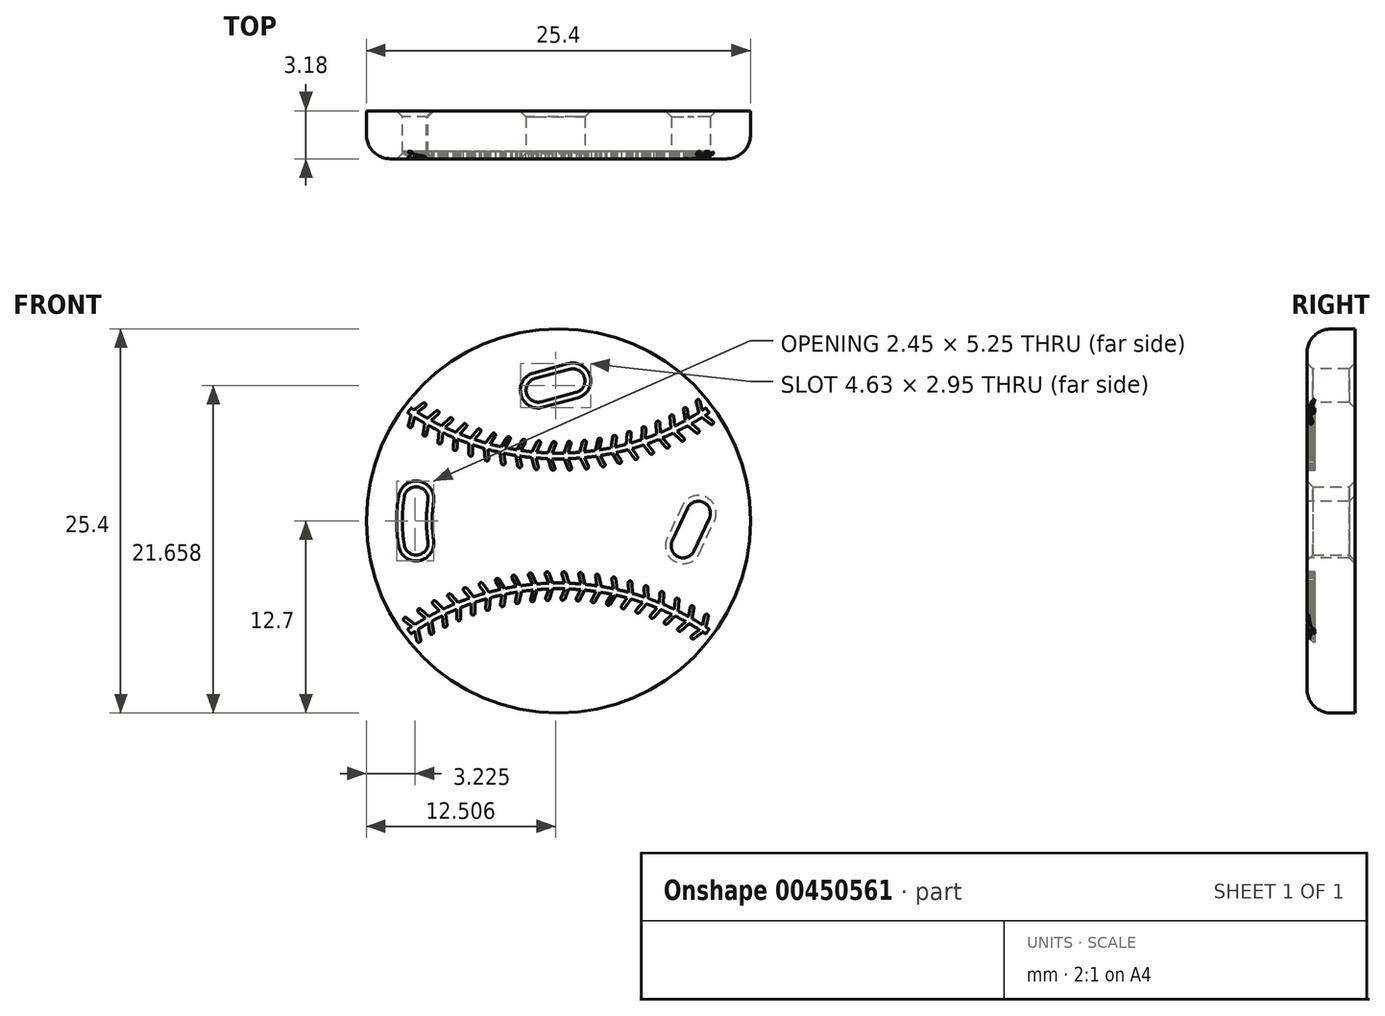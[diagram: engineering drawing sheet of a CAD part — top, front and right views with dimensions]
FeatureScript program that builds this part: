
annotation { "Feature Type Name" : "Feature", "Feature Type Description" : "" }
export const myFeature = defineFeature(function(context is Context, id is Id, definition is map)
    precondition{}
    {
        {
            var Q0;
            Q0=qCreatedBy(makeId("Front.planeOp"),FACE);
            var sketch = newSketch(context, id + "F0", { "sketchPlane" : qUnion([Q0])});
            skCircle(sketch, "E0", {"center": v(0, 0) * mm, "radius": 12.7 * mm});
            skArc(sketch, "E1", {"start": v(-10.2, 1.59) * mm, "mid": v(-10.32, 0) * mm, "end": v(-10.2, -1.59) * mm});
            skArc(sketch, "E2", {"start": v(-8.63, 1.34) * mm, "mid": v(-8.73, 0) * mm, "end": v(-8.63, -1.34) * mm});
            skArc(sketch, "E3", {"start": v(-8.63, 1.34) * mm, "mid": v(-9.29, 2.25) * mm, "end": v(-10.2, 1.59) * mm});
            skArc(sketch, "E4", {"start": v(-10.2, -1.59) * mm, "mid": v(-9.29, -2.25) * mm, "end": v(-8.63, -1.34) * mm});
            skLineSegment(sketch, "E5", {"start": v(-8.63, 0) * mm, "end": v(-8.63, -1.34) * mm, "construction": true});
            skPoint(sketch, "E6", {"position": v(-8.63, 0) * mm});
            skLineSegment(sketch, "E7", {"start": v(-8.63, 1.34) * mm, "end": v(-8.63, 0) * mm, "construction": true});
            skLineSegment(sketch, "E8", {"start": v(-8.63, 0) * mm, "end": v(0, 0) * mm, "construction": true});
            skSolve(sketch);
        }
        {
            var Q0;
            Q0=qSketchRegion(id+"F0",true);
            extrude(context, id + "F1", {"entities" : qUnion([Q0]), "depth" : 3.17 * mm});
        }
        {
            var Q0;
            Q0=makeQuery(id+"F1.opExtrude","CAP_EDGE",EDGE,{"disambiguationData":[OSD([sQuery(id+"F0.wireOp",EDGE,"E4")])],"isStart":false});
            var Q1;
            Q1=makeQuery(id+"F1.opExtrude","CAP_EDGE",EDGE,{"disambiguationData":[OSD([sQuery(id+"F0.wireOp",EDGE,"E2")])],"isStart":false});
            var Q2;
            Q2=makeQuery(id+"F1.opExtrude","CAP_EDGE",EDGE,{"disambiguationData":[OSD([sQuery(id+"F0.wireOp",EDGE,"E2")])],"isStart":true});
            chamfer(context, id + "F2", {"entities" : qUnion([Q0, Q1, Q2]), "width" : 0.38 * mm, "tangentPropagation" : true});
        }
        {
            var Q0;
            Q0=makeQuery(id+"F1.opExtrude","CAP_FACE",FACE,{"disambiguationData":[OSD([sQuery(id+"F0.wireOp",EDGE,"E0"),sQuery(id+"F0.wireOp",EDGE,"E1"),sQuery(id+"F0.wireOp",EDGE,"E2"),sQuery(id+"F0.wireOp",EDGE,"E3"),sQuery(id+"F0.wireOp",EDGE,"E4")])],"isStart":false});
            var sketch = newSketch(context, id + "F3", { "sketchPlane" : qUnion([Q0])});
            skLineSegment(sketch, "E9.bottom", {"start": v(0, -3.18) * mm, "end": v(-19.05, -3.18) * mm, "construction": true});
            skLineSegment(sketch, "E9.top", {"start": v(0, 3.18) * mm, "end": v(-19.05, 3.17) * mm, "construction": true});
            skLineSegment(sketch, "E9.left", {"start": v(0, -3.18) * mm, "end": v(0, 3.18) * mm, "construction": true});
            skLineSegment(sketch, "E9.right", {"start": v(-19.05, -3.18) * mm, "end": v(-19.05, 3.17) * mm, "construction": true});
            skSolve(sketch);
        }
        {
            var Q0;
            {var subQ4=sQuery(id+"F0.wireOp",EDGE,"E0");Q0=makeQuery(id+"F3.imprint","IMPRINT",FACE,{"disambiguationData":[TD([[makeQuery(id+"F3.imprint","IMPRINT",EDGE,{"derivedFrom":makeQuery(id+"F1.opExtrude","CAP_EDGE",EDGE,{"disambiguationData":[OSD([subQ4])],"isStart":false})}),1.0]])]});}
            var sketch = newSketch(context, id + "F4", { "sketchPlane" : qUnion([Q0])});
            skCircle(sketch, "E10", {"center": v(0, 0) * mm, "radius": 12.7 * mm, "construction": true});
            skArc(sketch, "E11", {"start": v(-10.1, 7.71) * mm, "mid": v(0, 4.49) * mm, "end": v(10.1, 7.71) * mm});
            skArc(sketch, "E12", {"start": v(-10.32, 7.4) * mm, "mid": v(0, 4.1) * mm, "end": v(10.32, 7.4) * mm});
            skLineSegment(sketch, "E13", {"start": v(0, 12.7) * mm, "end": v(0, 8.6) * mm, "construction": true});
            skLineSegment(sketch, "E14", {"start": v(0, 8.6) * mm, "end": v(0, 4.49) * mm, "construction": true});
            skLineSegment(sketch, "E15", {"start": v(0, 4.1) * mm, "end": v(0, 0) * mm, "construction": true});
            skArc(sketch, "E16", {"start": v(-10.1, 7.71) * mm, "mid": v(-10.2, 7.56) * mm, "end": v(-10.32, 7.4) * mm});
            skArc(sketch, "E17", {"start": v(10.32, 7.4) * mm, "mid": v(10.2, 7.56) * mm, "end": v(10.1, 7.71) * mm});
            skArc(sketch, "E18.MirrorCS", {"start": v(-10.1, -7.71) * mm, "mid": v(0, -4.49) * mm, "end": v(10.1, -7.71) * mm});
            skArc(sketch, "E19.MirrorCS", {"start": v(-10.32, -7.4) * mm, "mid": v(0, -4.1) * mm, "end": v(10.32, -7.4) * mm});
            skArc(sketch, "E20.MirrorCS", {"start": v(10.32, -7.4) * mm, "mid": v(10.2, -7.56) * mm, "end": v(10.1, -7.71) * mm});
            skArc(sketch, "E21.MirrorCS", {"start": v(-10.1, -7.71) * mm, "mid": v(-10.2, -7.56) * mm, "end": v(-10.32, -7.4) * mm});
            skSolve(sketch);
        }
        {
            var Q0;
            Q0=qSketchRegion(id+"F4",true);
            extrude(context, id + "F5", {"entities" : qUnion([Q0]), "operationType" : NewBodyOperationType.REMOVE, "oppositeDirection" : true, "depth" : 0.5 * mm});
        }
        {
            var Q0;
            {var subQ4=sQuery(id+"F0.wireOp",EDGE,"E0");Q0=makeQuery(id+"F3.imprint","IMPRINT",FACE,{"disambiguationData":[TD([[makeQuery(id+"F3.imprint","IMPRINT",EDGE,{"derivedFrom":makeQuery(id+"F1.opExtrude","CAP_EDGE",EDGE,{"disambiguationData":[OSD([subQ4])],"isStart":false})}),1.0]])]});}
            var sketch = newSketch(context, id + "F6", { "sketchPlane" : qUnion([Q0])});
            skCircle(sketch, "E22", {"center": v(0, 0) * mm, "radius": 12.7 * mm, "construction": true});
            skArc(sketch, "E23", {"start": v(10.32, -7.4) * mm, "mid": v(0, -4.1) * mm, "end": v(-10.32, -7.4) * mm, "construction": true});
            skArc(sketch, "E24", {"start": v(10.1, -7.71) * mm, "mid": v(0, -4.49) * mm, "end": v(-10.1, -7.71) * mm, "construction": true});
            skLineSegment(sketch, "E25", {"start": v(0, 0) * mm, "end": v(0, -4.1) * mm, "construction": true});
            skLineSegment(sketch, "E26", {"start": v(0, -4.49) * mm, "end": v(0, -8.6) * mm, "construction": true});
            skPoint(sketch, "E26.endSnap0", {"position": v(0, -4.49) * mm});
            skLineSegment(sketch, "E27", {"start": v(0, -8.6) * mm, "end": v(0, -12.7) * mm, "construction": true});
            skArc(sketch, "E28", {"start": v(-10.32, -7.4) * mm, "mid": v(-10.2, -7.56) * mm, "end": v(-10.1, -7.71) * mm, "construction": true});
            skArc(sketch, "E29", {"start": v(10.1, -7.71) * mm, "mid": v(10.2, -7.56) * mm, "end": v(10.32, -7.4) * mm, "construction": true});
            skArc(sketch, "E30", {"start": v(10.2, -7.56) * mm, "mid": v(0, -4.3) * mm, "end": v(-10.2, -7.56) * mm});
            skLineSegment(sketch, "E31", {"start": v(0, -4.1) * mm, "end": v(0, -4.3) * mm, "construction": true});
            skLineSegment(sketch, "E32", {"start": v(0, -4.3) * mm, "end": v(0, -4.49) * mm, "construction": true});
            skLineSegment(sketch, "E33", {"start": v(-9.79, -7.27) * mm, "end": v(-9.37, -7.93) * mm, "construction": true});
            skLineSegment(sketch, "E34", {"start": v(-10.2, -6.6) * mm, "end": v(-9.55, -7.11) * mm});
            skLineSegment(sketch, "E35", {"start": v(-9.55, -7.11) * mm, "end": v(-9.37, -7.93) * mm});
            skArc(sketch, "E36", {"start": v(-10.05, -6.4) * mm, "mid": v(-10.23, -6.43) * mm, "end": v(-10.2, -6.6) * mm});
            skLineSegment(sketch, "E37", {"start": v(-10.05, -6.4) * mm, "end": v(-9.32, -6.97) * mm});
            skLineSegment(sketch, "E38", {"start": v(-9.32, -6.97) * mm, "end": v(-9.12, -7.88) * mm});
            skArc(sketch, "E39", {"start": v(-9.37, -7.93) * mm, "mid": v(-9.22, -8.03) * mm, "end": v(-9.12, -7.88) * mm});
            skLineSegment(sketch, "E40", {"start": v(-10.2, -6.6) * mm, "end": v(-9.79, -7.27) * mm, "construction": true});
            skLineSegment(sketch, "E41.1.0", {"start": v(-9.27, -6.02) * mm, "end": v(-8.64, -6.57) * mm});
            skLineSegment(sketch, "E41.1.1", {"start": v(-8.64, -6.57) * mm, "end": v(-8.51, -7.4) * mm});
            skArc(sketch, "E41.1.2", {"start": v(-8.51, -7.4) * mm, "mid": v(-8.37, -7.5) * mm, "end": v(-8.26, -7.35) * mm});
            skLineSegment(sketch, "E41.1.3", {"start": v(-8.4, -6.44) * mm, "end": v(-8.26, -7.35) * mm});
            skLineSegment(sketch, "E41.1.4", {"start": v(-9.1, -5.83) * mm, "end": v(-8.4, -6.44) * mm});
            skArc(sketch, "E41.1.5", {"start": v(-9.1, -5.83) * mm, "mid": v(-9.28, -5.84) * mm, "end": v(-9.27, -6.02) * mm});
            skLineSegment(sketch, "E41.2.0", {"start": v(-8.3, -5.5) * mm, "end": v(-7.7, -6.07) * mm});
            skLineSegment(sketch, "E41.2.1", {"start": v(-7.7, -6.07) * mm, "end": v(-7.63, -6.9) * mm});
            skArc(sketch, "E41.2.2", {"start": v(-7.63, -6.9) * mm, "mid": v(-7.49, -7.02) * mm, "end": v(-7.37, -6.88) * mm});
            skLineSegment(sketch, "E41.2.3", {"start": v(-7.46, -5.96) * mm, "end": v(-7.37, -6.88) * mm});
            skLineSegment(sketch, "E41.2.4", {"start": v(-8.12, -5.31) * mm, "end": v(-7.46, -5.96) * mm});
            skArc(sketch, "E41.2.5", {"start": v(-8.12, -5.31) * mm, "mid": v(-8.3, -5.32) * mm, "end": v(-8.3, -5.5) * mm});
            skLineSegment(sketch, "E41.3.0", {"start": v(-7.3, -5.03) * mm, "end": v(-6.74, -5.64) * mm});
            skLineSegment(sketch, "E41.3.1", {"start": v(-6.74, -5.64) * mm, "end": v(-6.71, -6.48) * mm});
            skArc(sketch, "E41.3.2", {"start": v(-6.71, -6.48) * mm, "mid": v(-6.58, -6.6) * mm, "end": v(-6.46, -6.47) * mm});
            skLineSegment(sketch, "E41.3.3", {"start": v(-6.5, -5.54) * mm, "end": v(-6.46, -6.47) * mm});
            skLineSegment(sketch, "E41.3.4", {"start": v(-7.1, -4.86) * mm, "end": v(-6.5, -5.54) * mm});
            skArc(sketch, "E41.3.5", {"start": v(-7.1, -4.86) * mm, "mid": v(-7.29, -4.85) * mm, "end": v(-7.3, -5.03) * mm});
            skLineSegment(sketch, "E41.4.0", {"start": v(-6.27, -4.62) * mm, "end": v(-5.75, -5.26) * mm});
            skLineSegment(sketch, "E41.4.1", {"start": v(-5.75, -5.26) * mm, "end": v(-5.77, -6.1) * mm});
            skArc(sketch, "E41.4.2", {"start": v(-5.77, -6.1) * mm, "mid": v(-5.65, -6.23) * mm, "end": v(-5.52, -6.1) * mm});
            skLineSegment(sketch, "E41.4.3", {"start": v(-5.5, -5.18) * mm, "end": v(-5.52, -6.1) * mm});
            skLineSegment(sketch, "E41.4.4", {"start": v(-6.07, -4.46) * mm, "end": v(-5.5, -5.18) * mm});
            skArc(sketch, "E41.4.5", {"start": v(-6.07, -4.46) * mm, "mid": v(-6.25, -4.44) * mm, "end": v(-6.27, -4.62) * mm});
            skLineSegment(sketch, "E41.5.0", {"start": v(-5.22, -4.27) * mm, "end": v(-4.74, -4.95) * mm});
            skLineSegment(sketch, "E41.5.1", {"start": v(-4.74, -4.95) * mm, "end": v(-4.81, -5.78) * mm});
            skArc(sketch, "E41.5.2", {"start": v(-4.81, -5.78) * mm, "mid": v(-4.7, -5.92) * mm, "end": v(-4.56, -5.8) * mm});
            skLineSegment(sketch, "E41.5.3", {"start": v(-4.48, -4.88) * mm, "end": v(-4.56, -5.8) * mm});
            skLineSegment(sketch, "E41.5.4", {"start": v(-5.01, -4.13) * mm, "end": v(-4.48, -4.88) * mm});
            skArc(sketch, "E41.5.5", {"start": v(-5.01, -4.13) * mm, "mid": v(-5.19, -4.1) * mm, "end": v(-5.22, -4.27) * mm});
            skLineSegment(sketch, "E41.6.0", {"start": v(-4.15, -4) * mm, "end": v(-3.72, -4.7) * mm});
            skLineSegment(sketch, "E41.6.1", {"start": v(-3.72, -4.7) * mm, "end": v(-3.84, -5.52) * mm});
            skArc(sketch, "E41.6.2", {"start": v(-3.84, -5.52) * mm, "mid": v(-3.73, -5.67) * mm, "end": v(-3.58, -5.56) * mm});
            skLineSegment(sketch, "E41.6.3", {"start": v(-3.45, -4.64) * mm, "end": v(-3.58, -5.56) * mm});
            skLineSegment(sketch, "E41.6.4", {"start": v(-3.94, -3.86) * mm, "end": v(-3.45, -4.64) * mm});
            skArc(sketch, "E41.6.5", {"start": v(-3.94, -3.86) * mm, "mid": v(-4.11, -3.82) * mm, "end": v(-4.15, -4) * mm});
            skLineSegment(sketch, "E41.7.0", {"start": v(-3.07, -3.77) * mm, "end": v(-2.68, -4.5) * mm});
            skLineSegment(sketch, "E41.7.1", {"start": v(-2.68, -4.5) * mm, "end": v(-2.84, -5.32) * mm});
            skArc(sketch, "E41.7.2", {"start": v(-2.84, -5.32) * mm, "mid": v(-2.75, -5.47) * mm, "end": v(-2.6, -5.37) * mm});
            skLineSegment(sketch, "E41.7.3", {"start": v(-2.4, -4.46) * mm, "end": v(-2.6, -5.37) * mm});
            skLineSegment(sketch, "E41.7.4", {"start": v(-2.84, -3.65) * mm, "end": v(-2.4, -4.46) * mm});
            skArc(sketch, "E41.7.5", {"start": v(-2.84, -3.65) * mm, "mid": v(-3.02, -3.6) * mm, "end": v(-3.07, -3.77) * mm});
            skLineSegment(sketch, "E41.8.0", {"start": v(-1.97, -3.62) * mm, "end": v(-1.62, -4.37) * mm});
            skLineSegment(sketch, "E41.8.1", {"start": v(-1.62, -4.37) * mm, "end": v(-1.84, -5.18) * mm});
            skArc(sketch, "E41.8.2", {"start": v(-1.84, -5.18) * mm, "mid": v(-1.75, -5.34) * mm, "end": v(-1.6, -5.25) * mm});
            skLineSegment(sketch, "E41.8.3", {"start": v(-1.36, -4.35) * mm, "end": v(-1.6, -5.25) * mm});
            skLineSegment(sketch, "E41.8.4", {"start": v(-1.74, -3.51) * mm, "end": v(-1.36, -4.35) * mm});
            skArc(sketch, "E41.8.5", {"start": v(-1.74, -3.51) * mm, "mid": v(-1.91, -3.45) * mm, "end": v(-1.97, -3.62) * mm});
            skLineSegment(sketch, "E41.9.0", {"start": v(-0.87, -3.54) * mm, "end": v(-0.57, -4.3) * mm});
            skLineSegment(sketch, "E41.9.1", {"start": v(-0.57, -4.3) * mm, "end": v(-0.84, -5.1) * mm});
            skArc(sketch, "E41.9.2", {"start": v(-0.84, -5.1) * mm, "mid": v(-0.76, -5.26) * mm, "end": v(-0.6, -5.18) * mm});
            skLineSegment(sketch, "E41.9.3", {"start": v(-0.3, -4.3) * mm, "end": v(-0.6, -5.18) * mm});
            skLineSegment(sketch, "E41.9.4", {"start": v(-0.63, -3.44) * mm, "end": v(-0.3, -4.3) * mm});
            skArc(sketch, "E41.9.5", {"start": v(-0.63, -3.44) * mm, "mid": v(-0.8, -3.37) * mm, "end": v(-0.87, -3.54) * mm});
            skLineSegment(sketch, "E41.10.0", {"start": v(0.23, -3.52) * mm, "end": v(0.49, -4.3) * mm});
            skLineSegment(sketch, "E41.10.1", {"start": v(0.49, -4.3) * mm, "end": v(0.18, -5.08) * mm});
            skArc(sketch, "E41.10.2", {"start": v(0.18, -5.08) * mm, "mid": v(0.25, -5.24) * mm, "end": v(0.41, -5.17) * mm});
            skLineSegment(sketch, "E41.10.3", {"start": v(0.76, -4.31) * mm, "end": v(0.41, -5.17) * mm});
            skLineSegment(sketch, "E41.10.4", {"start": v(0.48, -3.44) * mm, "end": v(0.76, -4.31) * mm});
            skArc(sketch, "E41.10.5", {"start": v(0.48, -3.44) * mm, "mid": v(0.32, -3.36) * mm, "end": v(0.23, -3.52) * mm});
            skLineSegment(sketch, "E41.11.0", {"start": v(1.34, -3.56) * mm, "end": v(1.55, -4.36) * mm});
            skLineSegment(sketch, "E41.11.1", {"start": v(1.55, -4.36) * mm, "end": v(1.19, -5.12) * mm});
            skArc(sketch, "E41.11.2", {"start": v(1.19, -5.12) * mm, "mid": v(1.25, -5.29) * mm, "end": v(1.41, -5.23) * mm});
            skLineSegment(sketch, "E41.11.3", {"start": v(1.81, -4.4) * mm, "end": v(1.41, -5.23) * mm});
            skLineSegment(sketch, "E41.11.4", {"start": v(1.58, -3.5) * mm, "end": v(1.81, -4.4) * mm});
            skArc(sketch, "E41.11.5", {"start": v(1.58, -3.5) * mm, "mid": v(1.43, -3.4) * mm, "end": v(1.34, -3.56) * mm});
            skLineSegment(sketch, "E41.12.0", {"start": v(2.44, -3.68) * mm, "end": v(2.6, -4.49) * mm});
            skLineSegment(sketch, "E41.12.1", {"start": v(2.6, -4.49) * mm, "end": v(2.2, -5.22) * mm});
            skArc(sketch, "E41.12.2", {"start": v(2.2, -5.22) * mm, "mid": v(2.24, -5.4) * mm, "end": v(2.41, -5.34) * mm});
            skLineSegment(sketch, "E41.12.3", {"start": v(2.86, -4.53) * mm, "end": v(2.41, -5.34) * mm});
            skLineSegment(sketch, "E41.12.4", {"start": v(2.69, -3.63) * mm, "end": v(2.86, -4.53) * mm});
            skArc(sketch, "E41.12.5", {"start": v(2.69, -3.63) * mm, "mid": v(2.54, -3.53) * mm, "end": v(2.44, -3.68) * mm});
            skLineSegment(sketch, "E41.13.0", {"start": v(3.53, -3.86) * mm, "end": v(3.64, -4.68) * mm});
            skLineSegment(sketch, "E41.13.1", {"start": v(3.64, -4.68) * mm, "end": v(3.19, -5.38) * mm});
            skArc(sketch, "E41.13.2", {"start": v(3.19, -5.38) * mm, "mid": v(3.23, -5.56) * mm, "end": v(3.4, -5.52) * mm});
            skLineSegment(sketch, "E41.13.3", {"start": v(3.9, -4.74) * mm, "end": v(3.4, -5.52) * mm});
            skLineSegment(sketch, "E41.13.4", {"start": v(3.78, -3.82) * mm, "end": v(3.9, -4.74) * mm});
            skArc(sketch, "E41.13.5", {"start": v(3.78, -3.82) * mm, "mid": v(3.64, -3.71) * mm, "end": v(3.53, -3.86) * mm});
            skLineSegment(sketch, "E41.14.0", {"start": v(4.6, -4.1) * mm, "end": v(4.67, -4.93) * mm});
            skLineSegment(sketch, "E41.14.1", {"start": v(4.67, -4.93) * mm, "end": v(4.18, -5.6) * mm});
            skArc(sketch, "E41.14.2", {"start": v(4.18, -5.6) * mm, "mid": v(4.2, -5.78) * mm, "end": v(4.38, -5.75) * mm});
            skLineSegment(sketch, "E41.14.3", {"start": v(4.93, -5) * mm, "end": v(4.38, -5.75) * mm});
            skLineSegment(sketch, "E41.14.4", {"start": v(4.86, -4.08) * mm, "end": v(4.93, -5) * mm});
            skArc(sketch, "E41.14.5", {"start": v(4.86, -4.08) * mm, "mid": v(4.72, -3.97) * mm, "end": v(4.6, -4.1) * mm});
            skLineSegment(sketch, "E41.15.0", {"start": v(5.67, -4.41) * mm, "end": v(5.68, -5.24) * mm});
            skLineSegment(sketch, "E41.15.1", {"start": v(5.68, -5.24) * mm, "end": v(5.15, -5.89) * mm});
            skArc(sketch, "E41.15.2", {"start": v(5.15, -5.89) * mm, "mid": v(5.17, -6.06) * mm, "end": v(5.34, -6.05) * mm});
            skLineSegment(sketch, "E41.15.3", {"start": v(5.93, -5.33) * mm, "end": v(5.34, -6.05) * mm});
            skLineSegment(sketch, "E41.15.4", {"start": v(5.92, -4.4) * mm, "end": v(5.93, -5.33) * mm});
            skArc(sketch, "E41.15.5", {"start": v(5.92, -4.4) * mm, "mid": v(5.8, -4.28) * mm, "end": v(5.67, -4.41) * mm});
            skLineSegment(sketch, "E41.16.0", {"start": v(6.7, -4.78) * mm, "end": v(6.67, -5.6) * mm});
            skLineSegment(sketch, "E41.16.1", {"start": v(6.67, -5.6) * mm, "end": v(6.1, -6.22) * mm});
            skArc(sketch, "E41.16.2", {"start": v(6.1, -6.22) * mm, "mid": v(6.1, -6.4) * mm, "end": v(6.29, -6.4) * mm});
            skLineSegment(sketch, "E41.16.3", {"start": v(6.92, -5.71) * mm, "end": v(6.29, -6.4) * mm});
            skLineSegment(sketch, "E41.16.4", {"start": v(6.96, -4.8) * mm, "end": v(6.92, -5.71) * mm});
            skArc(sketch, "E41.16.5", {"start": v(6.96, -4.8) * mm, "mid": v(6.84, -4.66) * mm, "end": v(6.7, -4.78) * mm});
            skLineSegment(sketch, "E41.17.0", {"start": v(7.72, -5.22) * mm, "end": v(7.63, -6.04) * mm});
            skLineSegment(sketch, "E41.17.1", {"start": v(7.63, -6.04) * mm, "end": v(7.03, -6.62) * mm});
            skArc(sketch, "E41.17.2", {"start": v(7.03, -6.62) * mm, "mid": v(7.03, -6.8) * mm, "end": v(7.2, -6.8) * mm});
            skLineSegment(sketch, "E41.17.3", {"start": v(7.88, -6.16) * mm, "end": v(7.2, -6.8) * mm});
            skLineSegment(sketch, "E41.17.4", {"start": v(7.98, -5.24) * mm, "end": v(7.88, -6.16) * mm});
            skArc(sketch, "E41.17.5", {"start": v(7.98, -5.24) * mm, "mid": v(7.86, -5.1) * mm, "end": v(7.72, -5.22) * mm});
            skLineSegment(sketch, "E41.18.0", {"start": v(8.71, -5.71) * mm, "end": v(8.57, -6.53) * mm});
            skLineSegment(sketch, "E41.18.1", {"start": v(8.57, -6.53) * mm, "end": v(7.94, -7.07) * mm});
            skArc(sketch, "E41.18.2", {"start": v(7.94, -7.07) * mm, "mid": v(7.92, -7.25) * mm, "end": v(8.1, -7.26) * mm});
            skLineSegment(sketch, "E41.18.3", {"start": v(8.8, -6.66) * mm, "end": v(8.1, -7.26) * mm});
            skLineSegment(sketch, "E41.18.4", {"start": v(8.96, -5.75) * mm, "end": v(8.8, -6.66) * mm});
            skArc(sketch, "E41.18.5", {"start": v(8.96, -5.75) * mm, "mid": v(8.86, -5.6) * mm, "end": v(8.71, -5.71) * mm});
            skLineSegment(sketch, "E41.19.0", {"start": v(9.67, -6.27) * mm, "end": v(9.48, -7.07) * mm});
            skLineSegment(sketch, "E41.19.1", {"start": v(9.48, -7.07) * mm, "end": v(8.81, -7.57) * mm});
            skArc(sketch, "E41.19.2", {"start": v(8.81, -7.57) * mm, "mid": v(8.79, -7.75) * mm, "end": v(8.97, -7.78) * mm});
            skLineSegment(sketch, "E41.19.3", {"start": v(9.7, -7.22) * mm, "end": v(8.97, -7.78) * mm});
            skLineSegment(sketch, "E41.19.4", {"start": v(9.92, -6.32) * mm, "end": v(9.7, -7.22) * mm});
            skArc(sketch, "E41.19.5", {"start": v(9.92, -6.32) * mm, "mid": v(9.82, -6.17) * mm, "end": v(9.67, -6.27) * mm});
            skLineSegment(sketch, "E41.anchor1", {"start": v(0, -21.89) * mm, "end": v(-10.2, -6.6) * mm, "construction": true});
            skLineSegment(sketch, "E41.anchor2", {"start": v(0, -21.89) * mm, "end": v(9.67, -6.27) * mm, "construction": true});
            skSolve(sketch);
        }
        {
            var Q0;
            Q0=qSketchRegion(id+"F6",true);
            extrude(context, id + "F7", {"entities" : qUnion([Q0]), "operationType" : NewBodyOperationType.REMOVE, "oppositeDirection" : true, "depth" : 0.5 * mm});
        }
        {
            var Q0;
            {var subQ4=sQuery(id+"F0.wireOp",EDGE,"E0");Q0=makeQuery(id+"F3.imprint","IMPRINT",FACE,{"disambiguationData":[TD([[makeQuery(id+"F3.imprint","IMPRINT",EDGE,{"derivedFrom":makeQuery(id+"F1.opExtrude","CAP_EDGE",EDGE,{"disambiguationData":[OSD([subQ4])],"isStart":false})}),1.0]])]});}
            var sketch = newSketch(context, id + "F8", { "sketchPlane" : qUnion([Q0])});
            skCircle(sketch, "E42", {"center": v(0, 0) * mm, "radius": 12.7 * mm, "construction": true});
            skArc(sketch, "E43", {"start": v(-10.1, 7.71) * mm, "mid": v(0, 4.49) * mm, "end": v(10.1, 7.71) * mm, "construction": true});
            skArc(sketch, "E44", {"start": v(-10.32, 7.4) * mm, "mid": v(0, 4.1) * mm, "end": v(10.32, 7.4) * mm, "construction": true});
            skLineSegment(sketch, "E45", {"start": v(0, 12.7) * mm, "end": v(0, 8.6) * mm, "construction": true});
            skLineSegment(sketch, "E46", {"start": v(0, 8.6) * mm, "end": v(0, 4.49) * mm, "construction": true});
            skLineSegment(sketch, "E47", {"start": v(0, 4.1) * mm, "end": v(0, 0) * mm, "construction": true});
            skArc(sketch, "E48", {"start": v(-10.1, 7.71) * mm, "mid": v(-10.2, 7.56) * mm, "end": v(-10.32, 7.4) * mm, "construction": true});
            skArc(sketch, "E49", {"start": v(10.32, 7.4) * mm, "mid": v(10.2, 7.56) * mm, "end": v(10.1, 7.71) * mm, "construction": true});
            skArc(sketch, "E50", {"start": v(-10.2, 7.56) * mm, "mid": v(0, 4.3) * mm, "end": v(10.2, 7.56) * mm});
            skLineSegment(sketch, "E51", {"start": v(0, 4.49) * mm, "end": v(0, 4.3) * mm, "construction": true});
            skLineSegment(sketch, "E52", {"start": v(0, 4.3) * mm, "end": v(0, 4.1) * mm, "construction": true});
            skLineSegment(sketch, "E53", {"start": v(9.55, 7.11) * mm, "end": v(9.37, 7.93) * mm});
            skLineSegment(sketch, "E54", {"start": v(9.32, 6.97) * mm, "end": v(9.12, 7.88) * mm});
            skLineSegment(sketch, "E55", {"start": v(9.32, 6.97) * mm, "end": v(10.05, 6.4) * mm});
            skLineSegment(sketch, "E56", {"start": v(9.55, 7.11) * mm, "end": v(10.2, 6.6) * mm});
            skArc(sketch, "E57", {"start": v(9.37, 7.93) * mm, "mid": v(9.22, 8.03) * mm, "end": v(9.12, 7.88) * mm});
            skArc(sketch, "E58", {"start": v(10.05, 6.4) * mm, "mid": v(10.23, 6.43) * mm, "end": v(10.2, 6.6) * mm});
            skLineSegment(sketch, "E59", {"start": v(9.79, 7.27) * mm, "end": v(9.37, 7.93) * mm, "construction": true});
            skLineSegment(sketch, "E60", {"start": v(9.79, 7.27) * mm, "end": v(10.2, 6.6) * mm, "construction": true});
            skLineSegment(sketch, "E61.1.0", {"start": v(8.64, 6.57) * mm, "end": v(9.27, 6.02) * mm});
            skArc(sketch, "E61.1.1", {"start": v(9.1, 5.83) * mm, "mid": v(9.28, 5.84) * mm, "end": v(9.27, 6.02) * mm});
            skLineSegment(sketch, "E61.1.2", {"start": v(8.4, 6.44) * mm, "end": v(9.1, 5.83) * mm});
            skLineSegment(sketch, "E61.1.3", {"start": v(8.4, 6.44) * mm, "end": v(8.26, 7.35) * mm});
            skArc(sketch, "E61.1.4", {"start": v(8.51, 7.4) * mm, "mid": v(8.37, 7.5) * mm, "end": v(8.26, 7.35) * mm});
            skLineSegment(sketch, "E61.1.5", {"start": v(8.64, 6.57) * mm, "end": v(8.51, 7.4) * mm});
            skLineSegment(sketch, "E61.2.0", {"start": v(7.7, 6.07) * mm, "end": v(8.3, 5.5) * mm});
            skArc(sketch, "E61.2.1", {"start": v(8.12, 5.31) * mm, "mid": v(8.3, 5.32) * mm, "end": v(8.3, 5.5) * mm});
            skLineSegment(sketch, "E61.2.2", {"start": v(7.46, 5.96) * mm, "end": v(8.12, 5.31) * mm});
            skLineSegment(sketch, "E61.2.3", {"start": v(7.46, 5.96) * mm, "end": v(7.37, 6.88) * mm});
            skArc(sketch, "E61.2.4", {"start": v(7.63, 6.9) * mm, "mid": v(7.49, 7.02) * mm, "end": v(7.37, 6.88) * mm});
            skLineSegment(sketch, "E61.2.5", {"start": v(7.7, 6.07) * mm, "end": v(7.63, 6.9) * mm});
            skLineSegment(sketch, "E61.3.0", {"start": v(6.74, 5.64) * mm, "end": v(7.3, 5.03) * mm});
            skArc(sketch, "E61.3.1", {"start": v(7.1, 4.86) * mm, "mid": v(7.29, 4.85) * mm, "end": v(7.3, 5.03) * mm});
            skLineSegment(sketch, "E61.3.2", {"start": v(6.5, 5.54) * mm, "end": v(7.1, 4.86) * mm});
            skLineSegment(sketch, "E61.3.3", {"start": v(6.5, 5.54) * mm, "end": v(6.46, 6.47) * mm});
            skArc(sketch, "E61.3.4", {"start": v(6.71, 6.48) * mm, "mid": v(6.58, 6.6) * mm, "end": v(6.46, 6.47) * mm});
            skLineSegment(sketch, "E61.3.5", {"start": v(6.74, 5.64) * mm, "end": v(6.71, 6.48) * mm});
            skLineSegment(sketch, "E61.4.0", {"start": v(5.75, 5.26) * mm, "end": v(6.27, 4.62) * mm});
            skArc(sketch, "E61.4.1", {"start": v(6.07, 4.46) * mm, "mid": v(6.25, 4.44) * mm, "end": v(6.27, 4.62) * mm});
            skLineSegment(sketch, "E61.4.2", {"start": v(5.5, 5.18) * mm, "end": v(6.07, 4.46) * mm});
            skLineSegment(sketch, "E61.4.3", {"start": v(5.5, 5.18) * mm, "end": v(5.52, 6.1) * mm});
            skArc(sketch, "E61.4.4", {"start": v(5.77, 6.1) * mm, "mid": v(5.65, 6.23) * mm, "end": v(5.52, 6.1) * mm});
            skLineSegment(sketch, "E61.4.5", {"start": v(5.75, 5.26) * mm, "end": v(5.77, 6.1) * mm});
            skLineSegment(sketch, "E61.5.0", {"start": v(4.74, 4.95) * mm, "end": v(5.22, 4.27) * mm});
            skArc(sketch, "E61.5.1", {"start": v(5.01, 4.13) * mm, "mid": v(5.19, 4.1) * mm, "end": v(5.22, 4.27) * mm});
            skLineSegment(sketch, "E61.5.2", {"start": v(4.48, 4.88) * mm, "end": v(5.01, 4.13) * mm});
            skLineSegment(sketch, "E61.5.3", {"start": v(4.48, 4.88) * mm, "end": v(4.56, 5.8) * mm});
            skArc(sketch, "E61.5.4", {"start": v(4.81, 5.78) * mm, "mid": v(4.7, 5.92) * mm, "end": v(4.56, 5.8) * mm});
            skLineSegment(sketch, "E61.5.5", {"start": v(4.74, 4.95) * mm, "end": v(4.81, 5.78) * mm});
            skLineSegment(sketch, "E61.6.0", {"start": v(3.72, 4.7) * mm, "end": v(4.15, 4) * mm});
            skArc(sketch, "E61.6.1", {"start": v(3.94, 3.86) * mm, "mid": v(4.1, 3.82) * mm, "end": v(4.15, 4) * mm});
            skLineSegment(sketch, "E61.6.2", {"start": v(3.45, 4.64) * mm, "end": v(3.94, 3.86) * mm});
            skLineSegment(sketch, "E61.6.3", {"start": v(3.45, 4.64) * mm, "end": v(3.58, 5.56) * mm});
            skArc(sketch, "E61.6.4", {"start": v(3.84, 5.52) * mm, "mid": v(3.73, 5.67) * mm, "end": v(3.58, 5.56) * mm});
            skLineSegment(sketch, "E61.6.5", {"start": v(3.72, 4.7) * mm, "end": v(3.84, 5.52) * mm});
            skLineSegment(sketch, "E61.7.0", {"start": v(2.68, 4.5) * mm, "end": v(3.07, 3.77) * mm});
            skArc(sketch, "E61.7.1", {"start": v(2.84, 3.65) * mm, "mid": v(3.02, 3.6) * mm, "end": v(3.07, 3.77) * mm});
            skLineSegment(sketch, "E61.7.2", {"start": v(2.4, 4.46) * mm, "end": v(2.84, 3.65) * mm});
            skLineSegment(sketch, "E61.7.3", {"start": v(2.4, 4.46) * mm, "end": v(2.6, 5.37) * mm});
            skArc(sketch, "E61.7.4", {"start": v(2.84, 5.32) * mm, "mid": v(2.75, 5.47) * mm, "end": v(2.6, 5.37) * mm});
            skLineSegment(sketch, "E61.7.5", {"start": v(2.68, 4.5) * mm, "end": v(2.84, 5.32) * mm});
            skLineSegment(sketch, "E61.8.0", {"start": v(1.62, 4.37) * mm, "end": v(1.97, 3.62) * mm});
            skArc(sketch, "E61.8.1", {"start": v(1.74, 3.51) * mm, "mid": v(1.91, 3.45) * mm, "end": v(1.97, 3.62) * mm});
            skLineSegment(sketch, "E61.8.2", {"start": v(1.36, 4.35) * mm, "end": v(1.74, 3.51) * mm});
            skLineSegment(sketch, "E61.8.3", {"start": v(1.36, 4.35) * mm, "end": v(1.6, 5.25) * mm});
            skArc(sketch, "E61.8.4", {"start": v(1.84, 5.18) * mm, "mid": v(1.75, 5.34) * mm, "end": v(1.6, 5.25) * mm});
            skLineSegment(sketch, "E61.8.5", {"start": v(1.62, 4.37) * mm, "end": v(1.84, 5.18) * mm});
            skLineSegment(sketch, "E61.9.0", {"start": v(0.57, 4.3) * mm, "end": v(0.87, 3.54) * mm});
            skArc(sketch, "E61.9.1", {"start": v(0.63, 3.44) * mm, "mid": v(0.8, 3.37) * mm, "end": v(0.87, 3.54) * mm});
            skLineSegment(sketch, "E61.9.2", {"start": v(0.3, 4.3) * mm, "end": v(0.63, 3.44) * mm});
            skLineSegment(sketch, "E61.9.3", {"start": v(0.3, 4.3) * mm, "end": v(0.6, 5.18) * mm});
            skArc(sketch, "E61.9.4", {"start": v(0.84, 5.1) * mm, "mid": v(0.76, 5.26) * mm, "end": v(0.6, 5.18) * mm});
            skLineSegment(sketch, "E61.9.5", {"start": v(0.57, 4.3) * mm, "end": v(0.84, 5.1) * mm});
            skLineSegment(sketch, "E61.10.0", {"start": v(-0.49, 4.3) * mm, "end": v(-0.23, 3.52) * mm});
            skArc(sketch, "E61.10.1", {"start": v(-0.48, 3.44) * mm, "mid": v(-0.32, 3.36) * mm, "end": v(-0.23, 3.52) * mm});
            skLineSegment(sketch, "E61.10.2", {"start": v(-0.76, 4.31) * mm, "end": v(-0.48, 3.44) * mm});
            skLineSegment(sketch, "E61.10.3", {"start": v(-0.76, 4.31) * mm, "end": v(-0.41, 5.17) * mm});
            skArc(sketch, "E61.10.4", {"start": v(-0.18, 5.08) * mm, "mid": v(-0.25, 5.24) * mm, "end": v(-0.41, 5.17) * mm});
            skLineSegment(sketch, "E61.10.5", {"start": v(-0.49, 4.3) * mm, "end": v(-0.18, 5.08) * mm});
            skLineSegment(sketch, "E61.11.0", {"start": v(-1.55, 4.36) * mm, "end": v(-1.34, 3.56) * mm});
            skArc(sketch, "E61.11.1", {"start": v(-1.58, 3.5) * mm, "mid": v(-1.43, 3.4) * mm, "end": v(-1.34, 3.56) * mm});
            skLineSegment(sketch, "E61.11.2", {"start": v(-1.81, 4.4) * mm, "end": v(-1.58, 3.5) * mm});
            skLineSegment(sketch, "E61.11.3", {"start": v(-1.81, 4.4) * mm, "end": v(-1.41, 5.23) * mm});
            skArc(sketch, "E61.11.4", {"start": v(-1.19, 5.12) * mm, "mid": v(-1.25, 5.29) * mm, "end": v(-1.41, 5.23) * mm});
            skLineSegment(sketch, "E61.11.5", {"start": v(-1.55, 4.36) * mm, "end": v(-1.19, 5.12) * mm});
            skLineSegment(sketch, "E61.12.0", {"start": v(-2.6, 4.49) * mm, "end": v(-2.44, 3.68) * mm});
            skArc(sketch, "E61.12.1", {"start": v(-2.69, 3.63) * mm, "mid": v(-2.54, 3.53) * mm, "end": v(-2.44, 3.68) * mm});
            skLineSegment(sketch, "E61.12.2", {"start": v(-2.86, 4.53) * mm, "end": v(-2.69, 3.63) * mm});
            skLineSegment(sketch, "E61.12.3", {"start": v(-2.86, 4.53) * mm, "end": v(-2.41, 5.35) * mm});
            skArc(sketch, "E61.12.4", {"start": v(-2.2, 5.22) * mm, "mid": v(-2.24, 5.4) * mm, "end": v(-2.41, 5.35) * mm});
            skLineSegment(sketch, "E61.12.5", {"start": v(-2.6, 4.49) * mm, "end": v(-2.2, 5.22) * mm});
            skLineSegment(sketch, "E61.13.0", {"start": v(-3.64, 4.68) * mm, "end": v(-3.53, 3.86) * mm});
            skArc(sketch, "E61.13.1", {"start": v(-3.78, 3.82) * mm, "mid": v(-3.64, 3.71) * mm, "end": v(-3.53, 3.86) * mm});
            skLineSegment(sketch, "E61.13.2", {"start": v(-3.9, 4.74) * mm, "end": v(-3.78, 3.82) * mm});
            skLineSegment(sketch, "E61.13.3", {"start": v(-3.9, 4.74) * mm, "end": v(-3.4, 5.52) * mm});
            skArc(sketch, "E61.13.4", {"start": v(-3.19, 5.38) * mm, "mid": v(-3.23, 5.56) * mm, "end": v(-3.4, 5.52) * mm});
            skLineSegment(sketch, "E61.13.5", {"start": v(-3.64, 4.68) * mm, "end": v(-3.19, 5.38) * mm});
            skLineSegment(sketch, "E61.14.0", {"start": v(-4.67, 4.93) * mm, "end": v(-4.6, 4.1) * mm});
            skArc(sketch, "E61.14.1", {"start": v(-4.86, 4.08) * mm, "mid": v(-4.72, 3.97) * mm, "end": v(-4.6, 4.1) * mm});
            skLineSegment(sketch, "E61.14.2", {"start": v(-4.93, 5) * mm, "end": v(-4.86, 4.08) * mm});
            skLineSegment(sketch, "E61.14.3", {"start": v(-4.93, 5) * mm, "end": v(-4.38, 5.75) * mm});
            skArc(sketch, "E61.14.4", {"start": v(-4.18, 5.6) * mm, "mid": v(-4.2, 5.78) * mm, "end": v(-4.38, 5.75) * mm});
            skLineSegment(sketch, "E61.14.5", {"start": v(-4.67, 4.93) * mm, "end": v(-4.18, 5.6) * mm});
            skLineSegment(sketch, "E61.15.0", {"start": v(-5.68, 5.24) * mm, "end": v(-5.67, 4.41) * mm});
            skArc(sketch, "E61.15.1", {"start": v(-5.92, 4.4) * mm, "mid": v(-5.8, 4.28) * mm, "end": v(-5.67, 4.41) * mm});
            skLineSegment(sketch, "E61.15.2", {"start": v(-5.93, 5.33) * mm, "end": v(-5.92, 4.4) * mm});
            skLineSegment(sketch, "E61.15.3", {"start": v(-5.93, 5.33) * mm, "end": v(-5.34, 6.05) * mm});
            skArc(sketch, "E61.15.4", {"start": v(-5.15, 5.89) * mm, "mid": v(-5.17, 6.07) * mm, "end": v(-5.34, 6.05) * mm});
            skLineSegment(sketch, "E61.15.5", {"start": v(-5.68, 5.24) * mm, "end": v(-5.15, 5.89) * mm});
            skLineSegment(sketch, "E61.16.0", {"start": v(-6.67, 5.6) * mm, "end": v(-6.7, 4.78) * mm});
            skArc(sketch, "E61.16.1", {"start": v(-6.96, 4.8) * mm, "mid": v(-6.84, 4.66) * mm, "end": v(-6.7, 4.78) * mm});
            skLineSegment(sketch, "E61.16.2", {"start": v(-6.92, 5.71) * mm, "end": v(-6.96, 4.8) * mm});
            skLineSegment(sketch, "E61.16.3", {"start": v(-6.92, 5.71) * mm, "end": v(-6.29, 6.4) * mm});
            skArc(sketch, "E61.16.4", {"start": v(-6.1, 6.22) * mm, "mid": v(-6.1, 6.4) * mm, "end": v(-6.29, 6.4) * mm});
            skLineSegment(sketch, "E61.16.5", {"start": v(-6.67, 5.6) * mm, "end": v(-6.1, 6.22) * mm});
            skLineSegment(sketch, "E61.17.0", {"start": v(-7.63, 6.04) * mm, "end": v(-7.72, 5.22) * mm});
            skArc(sketch, "E61.17.1", {"start": v(-7.98, 5.24) * mm, "mid": v(-7.86, 5.1) * mm, "end": v(-7.72, 5.22) * mm});
            skLineSegment(sketch, "E61.17.2", {"start": v(-7.88, 6.16) * mm, "end": v(-7.98, 5.24) * mm});
            skLineSegment(sketch, "E61.17.3", {"start": v(-7.88, 6.16) * mm, "end": v(-7.2, 6.8) * mm});
            skArc(sketch, "E61.17.4", {"start": v(-7.03, 6.62) * mm, "mid": v(-7.03, 6.8) * mm, "end": v(-7.2, 6.8) * mm});
            skLineSegment(sketch, "E61.17.5", {"start": v(-7.63, 6.04) * mm, "end": v(-7.03, 6.62) * mm});
            skLineSegment(sketch, "E61.18.0", {"start": v(-8.57, 6.53) * mm, "end": v(-8.71, 5.71) * mm});
            skArc(sketch, "E61.18.1", {"start": v(-8.96, 5.75) * mm, "mid": v(-8.86, 5.6) * mm, "end": v(-8.71, 5.71) * mm});
            skLineSegment(sketch, "E61.18.2", {"start": v(-8.8, 6.66) * mm, "end": v(-8.96, 5.75) * mm});
            skLineSegment(sketch, "E61.18.3", {"start": v(-8.8, 6.66) * mm, "end": v(-8.1, 7.26) * mm});
            skArc(sketch, "E61.18.4", {"start": v(-7.94, 7.07) * mm, "mid": v(-7.92, 7.25) * mm, "end": v(-8.1, 7.26) * mm});
            skLineSegment(sketch, "E61.18.5", {"start": v(-8.57, 6.53) * mm, "end": v(-7.94, 7.07) * mm});
            skLineSegment(sketch, "E61.19.0", {"start": v(-9.48, 7.07) * mm, "end": v(-9.67, 6.27) * mm});
            skArc(sketch, "E61.19.1", {"start": v(-9.92, 6.32) * mm, "mid": v(-9.82, 6.17) * mm, "end": v(-9.67, 6.27) * mm});
            skLineSegment(sketch, "E61.19.2", {"start": v(-9.7, 7.22) * mm, "end": v(-9.92, 6.32) * mm});
            skLineSegment(sketch, "E61.19.3", {"start": v(-9.7, 7.22) * mm, "end": v(-8.97, 7.78) * mm});
            skArc(sketch, "E61.19.4", {"start": v(-8.81, 7.57) * mm, "mid": v(-8.79, 7.75) * mm, "end": v(-8.97, 7.78) * mm});
            skLineSegment(sketch, "E61.19.5", {"start": v(-9.48, 7.07) * mm, "end": v(-8.81, 7.57) * mm});
            skLineSegment(sketch, "E61.anchor1", {"start": v(0, 21.89) * mm, "end": v(9.55, 7.11) * mm, "construction": true});
            skLineSegment(sketch, "E61.anchor2", {"start": v(0, 21.89) * mm, "end": v(-9.48, 7.07) * mm, "construction": true});
            skSolve(sketch);
        }
        {
            var Q0;
            Q0=qSketchRegion(id+"F8",true);
            extrude(context, id + "F9", {"entities" : qUnion([Q0]), "operationType" : NewBodyOperationType.REMOVE, "oppositeDirection" : true, "depth" : 0.5 * mm});
        }
        {
            var Q0;
            Q0=qCreatedBy(makeId("Top.planeOp"),FACE);
            var sketch = newSketch(context, id + "F10", { "sketchPlane" : qUnion([Q0])});
            skArc(sketch, "E62", {"start": v(-12.7, -1.59) * mm, "mid": v(-12.24, -2.71) * mm, "end": v(-11.11, -3.18) * mm});
            skLineSegment(sketch, "E63", {"start": v(-12.7, -1.59) * mm, "end": v(-12.7, -3.18) * mm});
            skLineSegment(sketch, "E64", {"start": v(-12.7, -3.18) * mm, "end": v(-11.11, -3.18) * mm});
            skSolve(sketch);
        }
        {
            var Q0;
            Q0=qCreatedBy(makeId("Top.planeOp"),FACE);
            var sketch = newSketch(context, id + "F11", { "sketchPlane" : qUnion([Q0])});
            skLineSegment(sketch, "E65", {"start": v(0, 0) * mm, "end": v(0, -3.18) * mm});
            skSolve(sketch);
        }
        {
            var Q0;
            Q0=qSketchRegion(id+"F10",true);
            var Q1;
            Q1=sQuery(id+"F11.wireOp",EDGE,"E65");
            revolve(context, id + "F12", {"operationType" : NewBodyOperationType.REMOVE, "entities" : qUnion([Q0]), "axis" : qUnion([Q1]), "revolveType" : RevolveType.FULL, "oppositeDirection" : true});
        }
        {
            var Q0;
            {var subQ4=sQuery(id+"F0.wireOp",EDGE,"E0");Q0=makeQuery(id+"F3.imprint","IMPRINT",FACE,{"disambiguationData":[TD([[makeQuery(id+"F3.imprint","IMPRINT",EDGE,{"derivedFrom":makeQuery(id+"F1.opExtrude","CAP_EDGE",EDGE,{"disambiguationData":[OSD([subQ4])],"isStart":false})}),1.0]])]});}
            var sketch = newSketch(context, id + "F13", { "sketchPlane" : qUnion([Q0])});
            skLineSegment(sketch, "E66", {"start": v(8.54, 0.85) * mm, "end": v(7.53, -1.31) * mm});
            skLineSegment(sketch, "E67", {"start": v(7.92, -2.37) * mm, "end": v(7.92, -2.37) * mm});
            skLineSegment(sketch, "E68", {"start": v(8.97, -1.98) * mm, "end": v(9.98, 0.17) * mm});
            skLineSegment(sketch, "E69", {"start": v(9.6, 1.23) * mm, "end": v(9.6, 1.23) * mm});
            skPoint(sketch, "E70.visualSharp", {"position": v(8.87, 1.56) * mm});
            skArc(sketch, "E70.filletArc", {"start": v(9.6, 1.23) * mm, "mid": v(8.99, 1.26) * mm, "end": v(8.54, 0.85) * mm});
            skPoint(sketch, "E71.visualSharp", {"position": v(10.31, 0.9) * mm});
            skArc(sketch, "E71.filletArc", {"start": v(9.98, 0.17) * mm, "mid": v(10, 0.78) * mm, "end": v(9.6, 1.23) * mm});
            skPoint(sketch, "E72.visualSharp", {"position": v(8.63, -2.7) * mm});
            skArc(sketch, "E72.filletArc", {"start": v(7.92, -2.37) * mm, "mid": v(8.52, -2.4) * mm, "end": v(8.97, -1.98) * mm});
            skPoint(sketch, "E73.visualSharp", {"position": v(7.2, -2.03) * mm});
            skArc(sketch, "E73.filletArc", {"start": v(7.53, -1.31) * mm, "mid": v(7.5, -1.92) * mm, "end": v(7.92, -2.37) * mm});
            skLineSegment(sketch, "E74", {"start": v(7.53, -1.31) * mm, "end": v(8.97, -1.98) * mm, "construction": true});
            skSolve(sketch);
        }
        {
            var Q0;
            Q0=qSketchRegion(id+"F13",true);
            extrude(context, id + "F14", {"entities" : qUnion([Q0]), "operationType" : NewBodyOperationType.REMOVE, "oppositeDirection" : true, "depth" : 25.4 * mm});
        }
        {
            var Q0;
            Q0=makeQuery(id+"F14.boolean.opBoolean","COPY",EDGE,{"derivedFrom":makeQuery(id+"F14.opExtrude","CAP_EDGE",EDGE,{"disambiguationData":[OSD([sQuery(id+"F13.wireOp",EDGE,"E66")])],"isStart":true})});
            var Q1;
            Q1=makeQuery(id+"F14.boolean.opBoolean","INTERSECT",EDGE,{"derivedFrom":[makeQuery(id+"F1.opExtrude","CAP_FACE",FACE,{"disambiguationData":[OSD([sQuery(id+"F0.wireOp",EDGE,"E0"),sQuery(id+"F0.wireOp",EDGE,"E1"),sQuery(id+"F0.wireOp",EDGE,"E2"),sQuery(id+"F0.wireOp",EDGE,"E3"),sQuery(id+"F0.wireOp",EDGE,"E4")])],"isStart":true}),makeQuery(id+"F14.opExtrude","SWEPT_FACE",FACE,{"disambiguationData":[OSD([sQuery(id+"F13.wireOp",EDGE,"E66")])]})]});
            chamfer(context, id + "F15", {"entities" : qUnion([Q0, Q1]), "width" : 0.38 * mm, "tangentPropagation" : true});
        }
        {
            var Q0;
            {var subQ4=sQuery(id+"F0.wireOp",EDGE,"E0");Q0=makeQuery(id+"F3.imprint","IMPRINT",FACE,{"disambiguationData":[TD([[makeQuery(id+"F3.imprint","IMPRINT",EDGE,{"derivedFrom":makeQuery(id+"F1.opExtrude","CAP_EDGE",EDGE,{"disambiguationData":[OSD([subQ4])],"isStart":false})}),1.0]])]});}
            var sketch = newSketch(context, id + "F16", { "sketchPlane" : qUnion([Q0])});
            skLineSegment(sketch, "E75", {"start": v(-1.55, 9.42) * mm, "end": v(0.75, 10.03) * mm});
            skLineSegment(sketch, "E76", {"start": v(1.72, 9.47) * mm, "end": v(1.72, 9.47) * mm});
            skLineSegment(sketch, "E77", {"start": v(1.16, 8.5) * mm, "end": v(-1.14, 7.88) * mm});
            skLineSegment(sketch, "E78", {"start": v(-2.11, 8.44) * mm, "end": v(-2.11, 8.44) * mm});
            skPoint(sketch, "E79.visualSharp", {"position": v(-2.32, 9.21) * mm});
            skArc(sketch, "E79.filletArc", {"start": v(-1.55, 9.42) * mm, "mid": v(-2.03, 9.05) * mm, "end": v(-2.11, 8.44) * mm});
            skPoint(sketch, "E80.visualSharp", {"position": v(1.52, 10.24) * mm});
            skArc(sketch, "E80.filletArc", {"start": v(1.72, 9.47) * mm, "mid": v(1.35, 9.95) * mm, "end": v(0.75, 10.03) * mm});
            skPoint(sketch, "E81.visualSharp", {"position": v(1.93, 8.7) * mm});
            skArc(sketch, "E81.filletArc", {"start": v(1.16, 8.5) * mm, "mid": v(1.64, 8.87) * mm, "end": v(1.72, 9.47) * mm});
            skPoint(sketch, "E82.visualSharp", {"position": v(-1.9, 7.68) * mm});
            skArc(sketch, "E82.filletArc", {"start": v(-2.11, 8.44) * mm, "mid": v(-1.74, 7.96) * mm, "end": v(-1.14, 7.88) * mm});
            skSolve(sketch);
        }
        {
            var Q0;
            Q0=qSketchRegion(id+"F16",true);
            extrude(context, id + "F17", {"entities" : qUnion([Q0]), "operationType" : NewBodyOperationType.REMOVE, "oppositeDirection" : true, "depth" : 25.4 * mm});
        }
        {
            var Q0;
            Q0=makeQuery(id+"F17.boolean.opBoolean","COPY",FACE,{"derivedFrom":makeQuery(id+"F17.opExtrude","SWEPT_FACE",FACE,{"disambiguationData":[OSD([sQuery(id+"F16.wireOp",EDGE,"E77")])]})});
            chamfer(context, id + "F18", {"entities" : qUnion([Q0]), "width" : 0.38 * mm, "tangentPropagation" : true});
        }
    });
